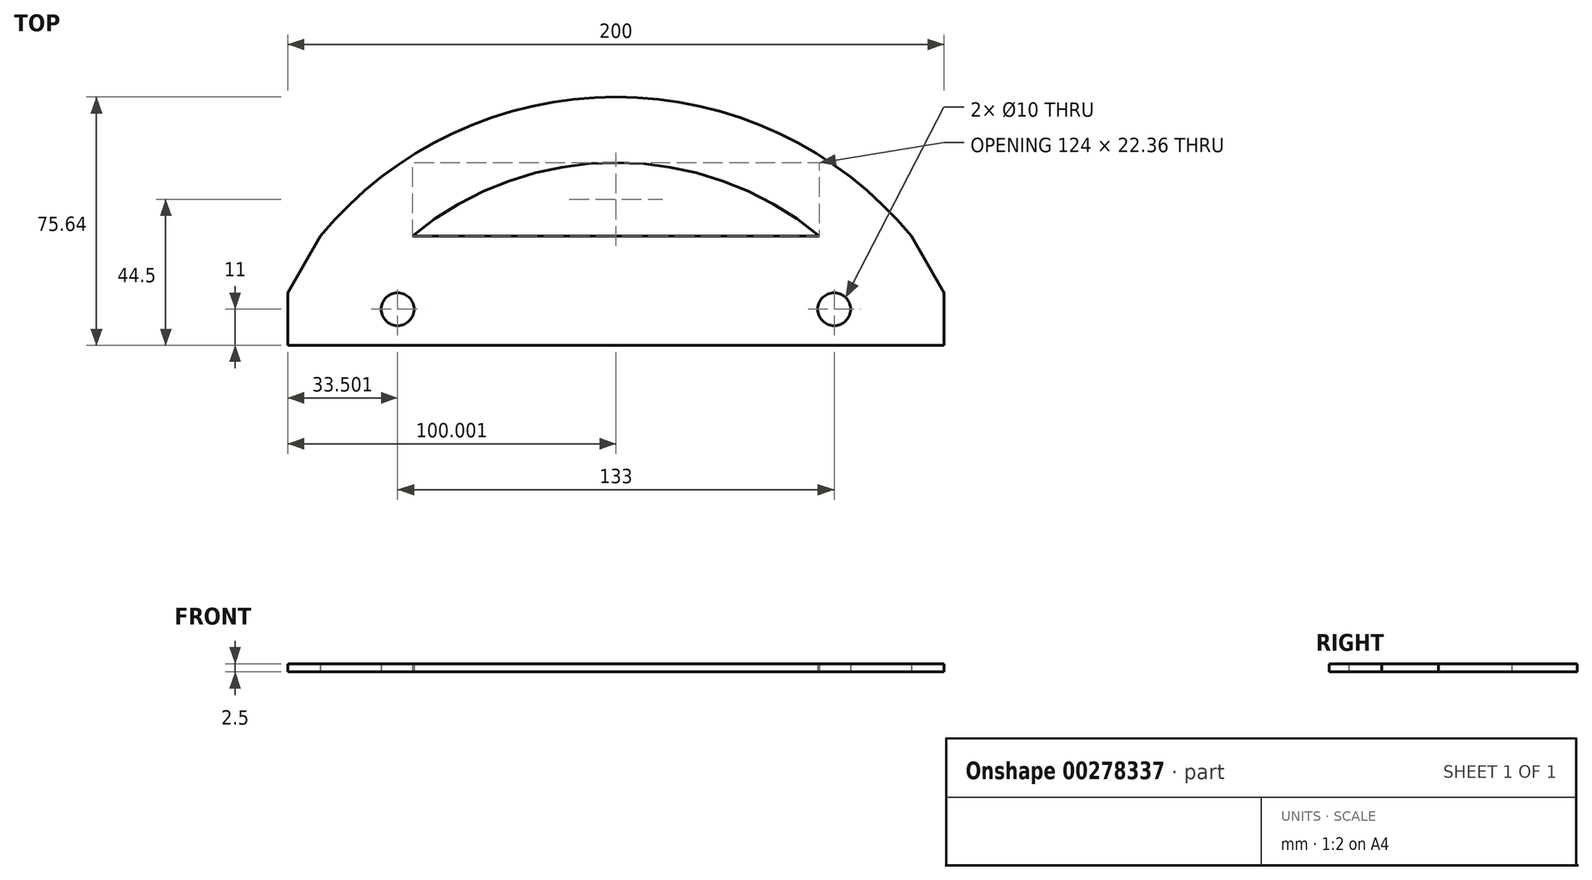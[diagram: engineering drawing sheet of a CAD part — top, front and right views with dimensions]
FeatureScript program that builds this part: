
annotation { "Feature Type Name" : "Feature", "Feature Type Description" : "" }
export const myFeature = defineFeature(function(context is Context, id is Id, definition is map)
    precondition{}
    {
        {
            var Q0;
            Q0=qCreatedBy(makeId("Top.planeOp"),FACE);
            var sketch = newSketch(context, id + "F0", { "sketchPlane" : qUnion([Q0])});
            skLineSegment(sketch, "E0.top", {"start": v(-97.14, -33.32) * mm, "end": v(102.86, -33.32) * mm});
            skLineSegment(sketch, "E0.left", {"start": v(-97.14, -17.32) * mm, "end": v(-97.14, -33.32) * mm});
            skLineSegment(sketch, "E0.right", {"start": v(102.86, -17.32) * mm, "end": v(102.86, -33.32) * mm});
            skCircle(sketch, "E1", {"center": v(-63.64, -22.32) * mm, "radius": 5 * mm});
            skCircle(sketch, "E2", {"center": v(69.36, -22.32) * mm, "radius": 5 * mm});
            skPoint(sketch, "E3", {"position": v(-63.64, -33.32) * mm});
            skPoint(sketch, "E4", {"position": v(69.36, -33.32) * mm});
            skLineSegment(sketch, "E5", {"start": v(-63.64, -33.32) * mm, "end": v(-97.14, -33.32) * mm});
            skLineSegment(sketch, "E6", {"start": v(69.36, -33.32) * mm, "end": v(102.86, -33.32) * mm});
            skLineSegment(sketch, "E7", {"start": v(-97.14, -17.32) * mm, "end": v(-87.14, 0) * mm});
            skLineSegment(sketch, "E8", {"start": v(102.86, -17.32) * mm, "end": v(92.86, 0) * mm});
            skArc(sketch, "E9", {"start": v(92.86, 0) * mm, "mid": v(2.86, 42.32) * mm, "end": v(-87.14, 0) * mm});
            skPoint(sketch, "E10", {"position": v(-59.14, 0) * mm});
            skPoint(sketch, "E11", {"position": v(64.86, 0) * mm});
            skArc(sketch, "E12", {"start": v(64.86, 0) * mm, "mid": v(2.86, 22.36) * mm, "end": v(-59.14, 0) * mm});
            skLineSegment(sketch, "E13", {"start": v(-59.14, 0) * mm, "end": v(64.86, 0) * mm});
            skSolve(sketch);
        }
        {
            var Q0;
            Q0=makeQuery(id+"F0.imprint","IMPRINT",FACE,{"disambiguationData":[TD([[makeQuery(id+"F0.imprint","IMPRINT",EDGE,{"derivedFrom":sQuery(id+"F0.wireOp",EDGE,"E0.top")}),1.0]])]});
            extrude(context, id + "F1", {"entities" : qUnion([Q0]), "depth" : 2.5 * mm});
        }
    });
